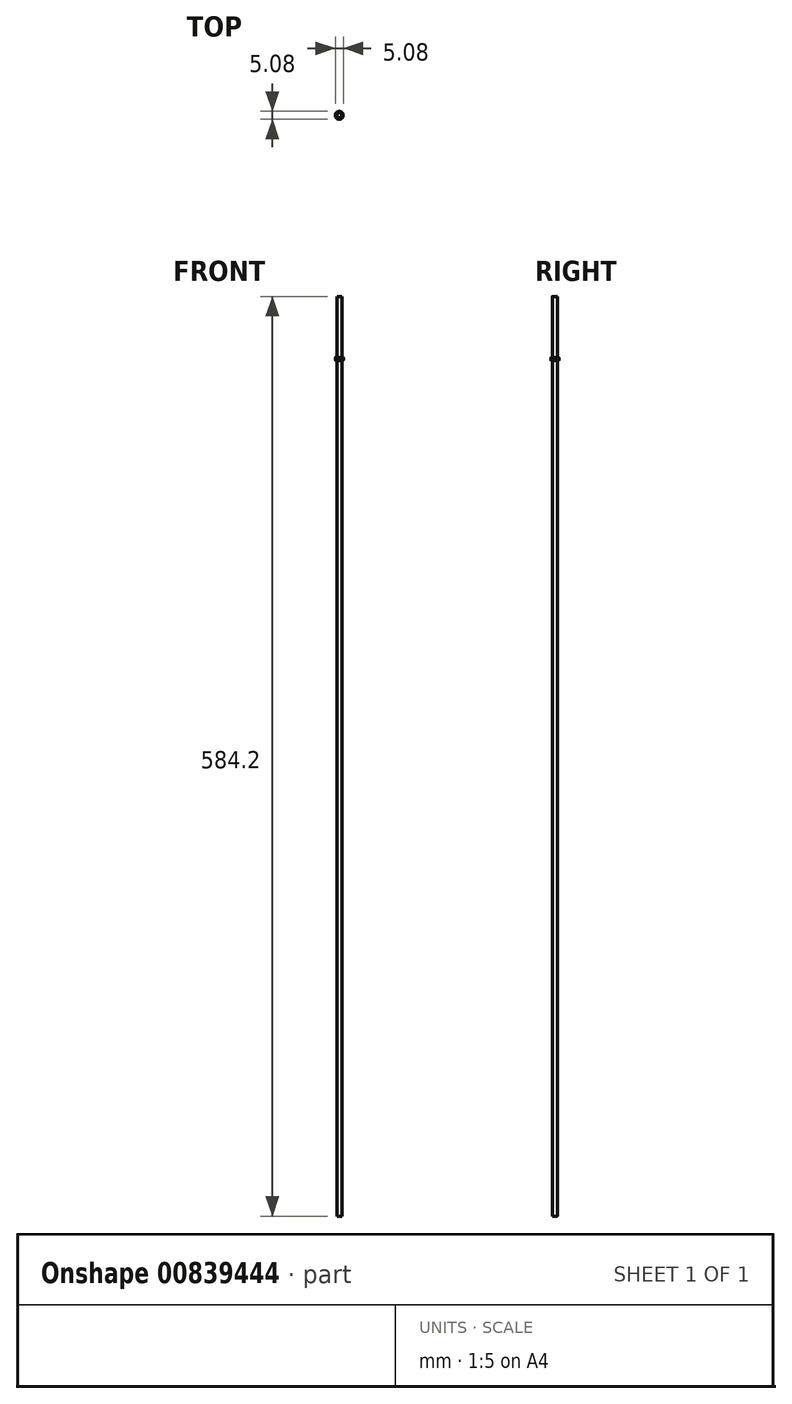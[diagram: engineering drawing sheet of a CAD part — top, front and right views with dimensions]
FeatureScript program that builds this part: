
annotation { "Feature Type Name" : "Feature", "Feature Type Description" : "" }
export const myFeature = defineFeature(function(context is Context, id is Id, definition is map)
    precondition{}
    {
        {
            var Q0;
            Q0=qCreatedBy(makeId("Top.planeOp"),FACE);
            var sketch = newSketch(context, id + "F0", { "sketchPlane" : qUnion([Q0])});
            skCircle(sketch, "E0", {"center": v(0, 0) * mm, "radius": 1.59 * mm});
            skSolve(sketch);
        }
        {
            var Q0;
            Q0 = qSketchRegion(id + "F0", true);
            extrude(context, id + "F1", {"entities" : qUnion([Q0]), "depth" : 584.2 * mm, "offsetDistance" : 25.4 * mm, "symmetric" : true});
        }
        {
            var Q0;
            Q0=makeQuery(id+"F1.opExtrude","CAP_FACE",FACE,{"disambiguationData":[OSD([sQuery(id+"F0.wireOp",EDGE,"E0")])],"isStart":false});
            cPlane(context, id + "F2", {"entities" : qUnion([Q0]), "cplaneType" : CPlaneType.OFFSET, "offset" : 40.64 * mm, "oppositeDirection" : true, "width" : 152.4 * mm, "height" : 152.4 * mm});
        }
        {
            var Q0;
            Q0=qCreatedBy(id+"F2.planeOp",FACE);
            var sketch = newSketch(context, id + "F3", { "sketchPlane" : qUnion([Q0])});
            skCircle(sketch, "E1", {"center": v(0, 0) * mm, "radius": 2.54 * mm});
            skSolve(sketch);
        }
        {
            var Q0;
            Q0 = qSketchRegion(id + "F3", true);
            extrude(context, id + "F4", {"entities" : qUnion([Q0]), "operationType" : NewBodyOperationType.ADD, "depth" : 1.9 * mm, "offsetDistance" : 25.4 * mm});
        }
        {
            var Q0;
            Q0=makeQuery(id+"F4.opExtrude","CAP_EDGE",EDGE,{"disambiguationData":[OSD([sQuery(id+"F3.wireOp",EDGE,"E1")])],"isStart":false});
            var Q1;
            Q1=makeQuery(id+"F4.opExtrude","CAP_EDGE",EDGE,{"disambiguationData":[OSD([sQuery(id+"F3.wireOp",EDGE,"E1")])],"isStart":true});
            fillet(context, id + "F5", {"entities" : qUnion([Q0, Q1]), "tangentPropagation" : true, "radius" : 0.25 * mm, "defaultsChanged" : false, "vertexSettings" : [], "allowEdgeOverflow" : false});
        }
    });
